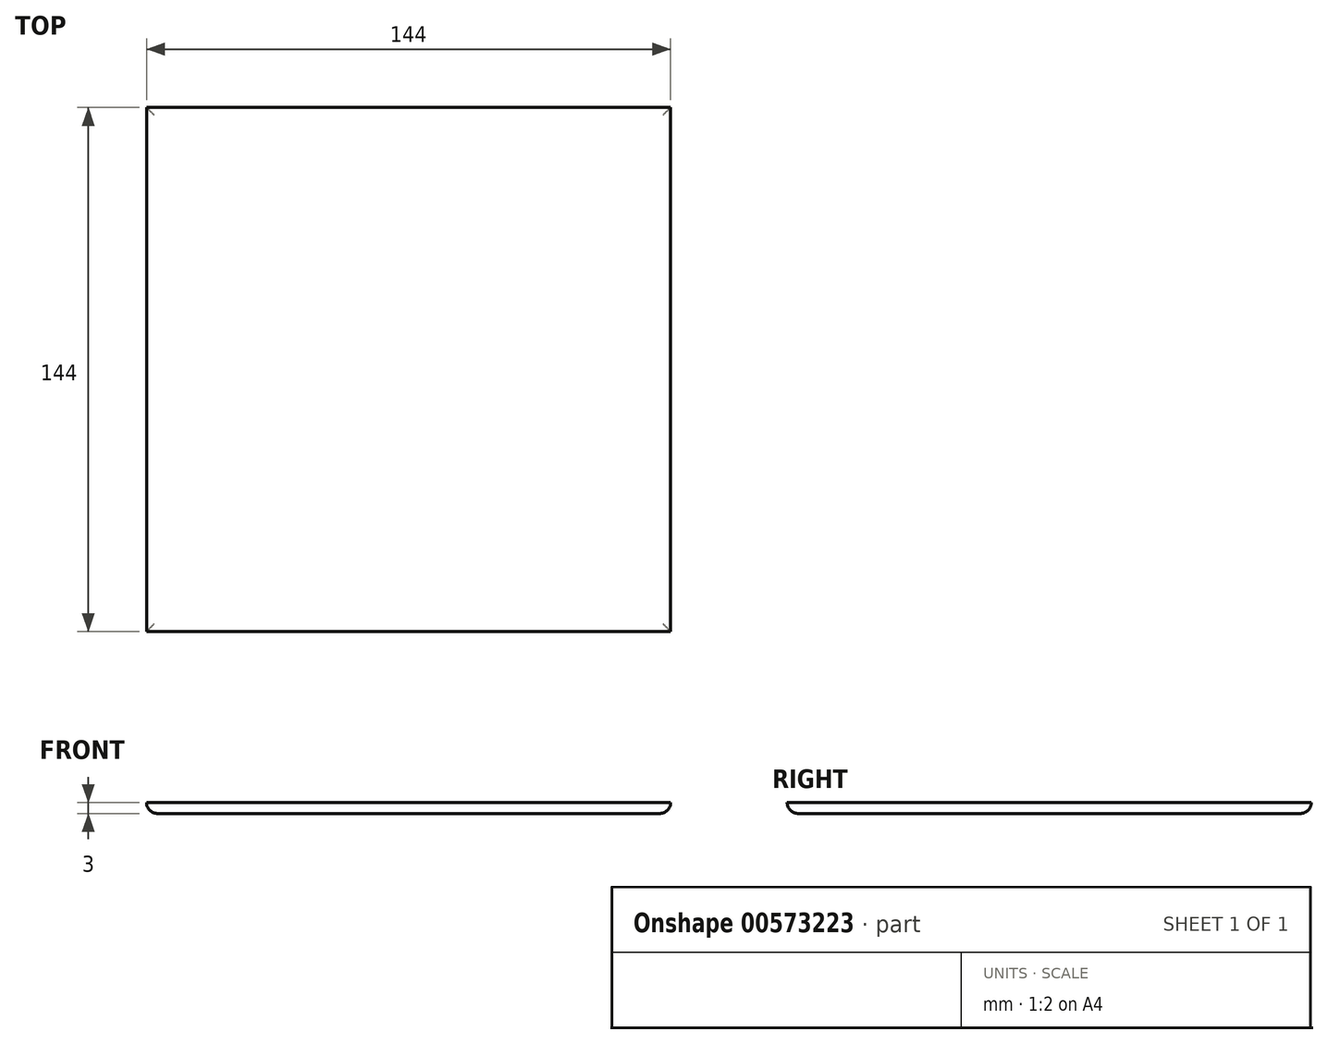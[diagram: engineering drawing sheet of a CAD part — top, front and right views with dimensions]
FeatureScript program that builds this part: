
annotation { "Feature Type Name" : "Feature", "Feature Type Description" : "" }
export const myFeature = defineFeature(function(context is Context, id is Id, definition is map)
    precondition{}
    {
        {
            var Q0;
            Q0=qCreatedBy(makeId("Top.planeOp"),FACE);
            var sketch = newSketch(context, id + "F0", { "sketchPlane" : qUnion([Q0])});
            skLineSegment(sketch, "E0.bottom", {"start": v(0, 0) * mm, "end": v(144, 0) * mm});
            skLineSegment(sketch, "E0.top", {"start": v(0, -144) * mm, "end": v(144, -144) * mm});
            skLineSegment(sketch, "E0.left", {"start": v(0, 0) * mm, "end": v(0, -144) * mm});
            skLineSegment(sketch, "E0.right", {"start": v(144, 0) * mm, "end": v(144, -144) * mm});
            skSolve(sketch);
        }
        {
            var Q0;
            Q0 = qSketchRegion(id + "F0", true);
            extrude(context, id + "F1", {"entities" : qUnion([Q0]), "depth" : 3 * mm, "offsetDistance" : 25 * mm});
        }
        {
            var Q0;
            Q0=makeQuery(id+"F1.opExtrude","CAP_FACE",FACE,{"disambiguationData":[OSD([sQuery(id+"F0.wireOp",EDGE,"E0.bottom"),sQuery(id+"F0.wireOp",EDGE,"E0.top"),sQuery(id+"F0.wireOp",EDGE,"E0.left"),sQuery(id+"F0.wireOp",EDGE,"E0.right")])],"isStart":true});
            fillet(context, id + "F2", {"entities" : qUnion([Q0]), "radius" : 3 * mm, "tangentPropagation" : true, "allowEdgeOverflow" : false});
        }
    });
